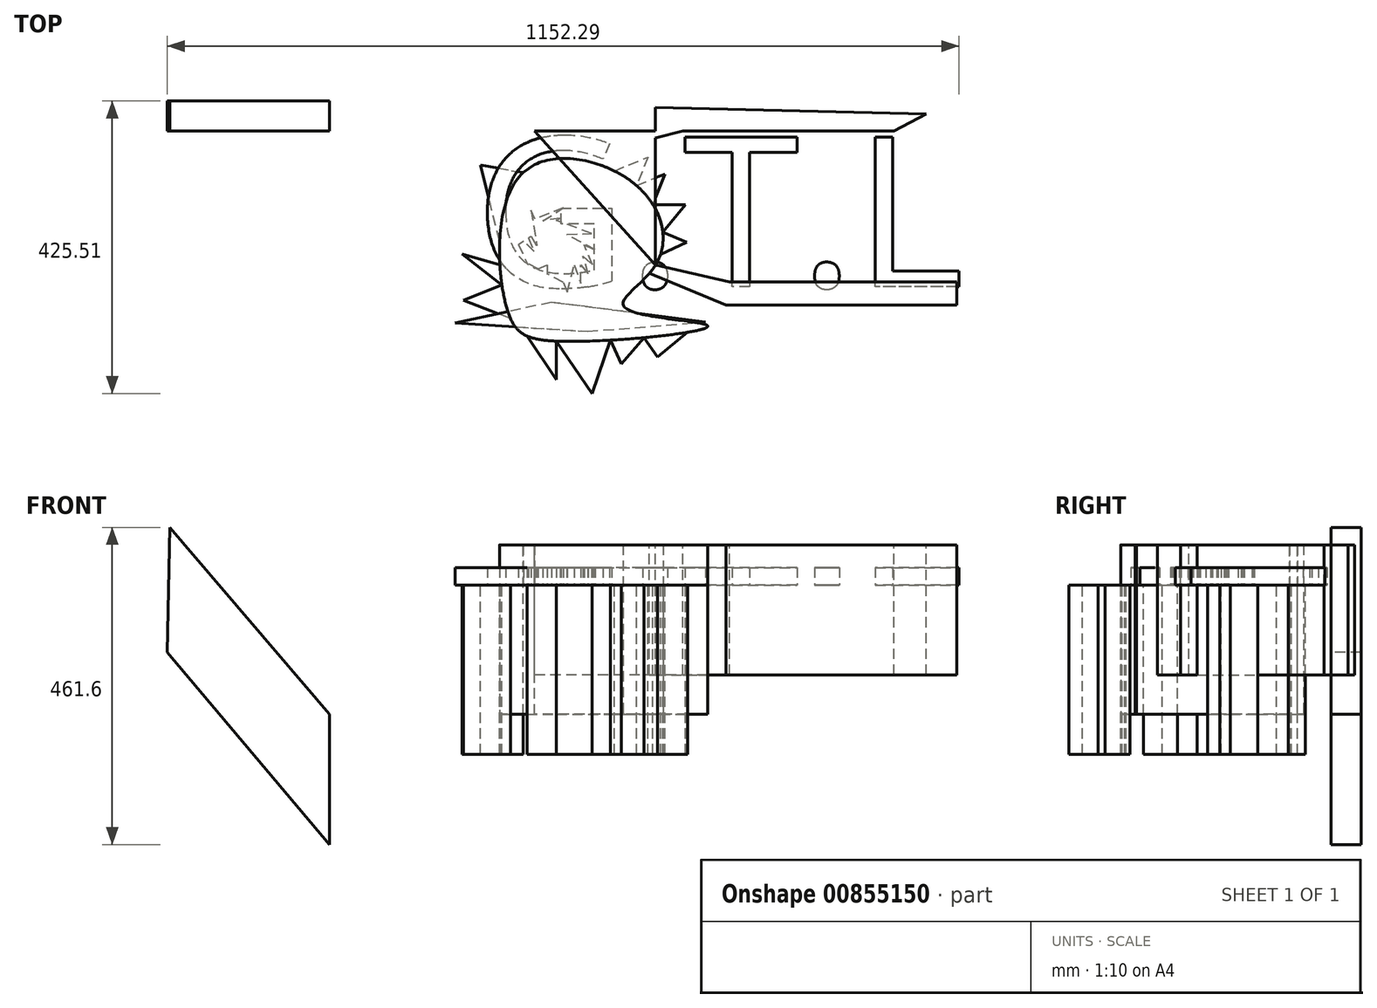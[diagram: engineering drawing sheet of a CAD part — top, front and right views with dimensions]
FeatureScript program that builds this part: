
annotation { "Feature Type Name" : "Feature", "Feature Type Description" : "" }
export const myFeature = defineFeature(function(context is Context, id is Id, definition is map)
    precondition{}
    {
        {
            var Q0;
            Q0=qCreatedBy(makeId("Top.planeOp"),FACE);
            var sketch = newSketch(context, id + "F0", { "sketchPlane" : qUnion([Q0])});
            skCircle(sketch, "E0.cCircle", {"center": v(-8.8, 21.17) * mm, "radius": 64.91 * mm, "construction": true});
            skLineSegment(sketch, "E0.0", {"start": v(25.69, -33.83) * mm, "end": v(-73.67, 18.8) * mm});
            skLineSegment(sketch, "E0.1", {"start": v(-73.67, 18.8) * mm, "end": v(21.58, 78.53) * mm});
            skLineSegment(sketch, "E0.2", {"start": v(21.58, 78.53) * mm, "end": v(25.69, -33.83) * mm});
            skLineSegment(sketch, "E1", {"start": v(-8.8, -43.75) * mm, "end": v(0, 0) * mm});
            skLineSegment(sketch, "E2", {"start": v(0, 0) * mm, "end": v(15.37, -39.08) * mm});
            skLineSegment(sketch, "E3", {"start": v(15.37, -39.08) * mm, "end": v(25.69, 0) * mm});
            skLineSegment(sketch, "E4", {"start": v(25.69, 0) * mm, "end": v(35.5, -26.28) * mm});
            skLineSegment(sketch, "E5", {"start": v(35.5, -26.28) * mm, "end": v(35.5, 0) * mm});
            skLineSegment(sketch, "E6", {"start": v(35.5, 0) * mm, "end": v(46.3, -13.14) * mm});
            skPoint(sketch, "E6.endSnap0", {"position": v(35.5, -13.14) * mm});
            skLineSegment(sketch, "E7", {"start": v(46.3, -13.14) * mm, "end": v(38.83, 12.73) * mm});
            skLineSegment(sketch, "E8", {"start": v(38.83, 12.73) * mm, "end": v(52.57, 0) * mm});
            skLineSegment(sketch, "E9", {"start": v(52.57, 0) * mm, "end": v(40.33, 29.47) * mm});
            skLineSegment(sketch, "E10", {"start": v(40.33, 29.47) * mm, "end": v(56.1, 22.26) * mm});
            skLineSegment(sketch, "E11", {"start": v(56.1, 22.26) * mm, "end": v(15.03, 44.44) * mm});
            skLineSegment(sketch, "E12", {"start": v(15.03, 44.44) * mm, "end": v(51.27, 45.76) * mm});
            skLineSegment(sketch, "E13", {"start": v(51.27, 45.76) * mm, "end": v(0, 65) * mm});
            skLineSegment(sketch, "E14", {"start": v(0, 65) * mm, "end": v(30.84, 72.57) * mm});
            skLineSegment(sketch, "E15", {"start": v(30.84, 72.57) * mm, "end": v(-20.16, 64.2) * mm});
            skLineSegment(sketch, "E16", {"start": v(-20.16, 64.2) * mm, "end": v(10.12, 83.26) * mm});
            skLineSegment(sketch, "E17", {"start": v(10.12, 83.26) * mm, "end": v(-31.54, 66.7) * mm});
            skLineSegment(sketch, "E18", {"start": v(-31.54, 66.7) * mm, "end": v(-36.73, 79.76) * mm});
            skLineSegment(sketch, "E19", {"start": v(-36.73, 79.76) * mm, "end": v(-28.6, 28.3) * mm});
            skLineSegment(sketch, "E20", {"start": v(-28.6, 28.3) * mm, "end": v(-52.81, 68.88) * mm});
            skLineSegment(sketch, "E21", {"start": v(-52.81, 68.88) * mm, "end": v(-32.66, 19.88) * mm});
            skPoint(sketch, "E21.endSnap0", {"position": v(-32.66, 54.03) * mm});
            skLineSegment(sketch, "E22", {"start": v(-32.66, 19.88) * mm, "end": v(-65.53, 52.72) * mm});
            skLineSegment(sketch, "E23", {"start": v(-65.53, 52.72) * mm, "end": v(-42.74, 2.41) * mm});
            skPoint(sketch, "E23.endSnap0", {"position": v(-42.74, 44.38) * mm});
            skLineSegment(sketch, "E24", {"start": v(-42.74, 2.41) * mm, "end": v(-70.94, 2.41) * mm});
            skLineSegment(sketch, "E25", {"start": v(-70.94, 2.41) * mm, "end": v(-23.99, -7.52) * mm});
            skLineSegment(sketch, "E26", {"start": v(-23.99, -7.52) * mm, "end": v(-59.26, -19.66) * mm});
            skLineSegment(sketch, "E27", {"start": v(-59.26, -19.66) * mm, "end": v(-13.56, 0) * mm});
            skLineSegment(sketch, "E28", {"start": v(-13.56, 0) * mm, "end": v(-32.2, -39.38) * mm});
            skLineSegment(sketch, "E29", {"start": v(-32.2, -39.38) * mm, "end": v(-13.56, 0) * mm});
            skLineSegment(sketch, "E30", {"start": v(-13.56, 0) * mm, "end": v(-13.56, -50.7) * mm});
            skLineSegment(sketch, "E31", {"start": v(-13.56, -50.7) * mm, "end": v(-13.56, -25.35) * mm});
            skLineSegment(sketch, "E32", {"start": v(-13.56, -25.35) * mm, "end": v(-7.33, -54.3) * mm});
            skLineSegment(sketch, "E33", {"start": v(-7.33, -54.3) * mm, "end": v(-147.81, -84.54) * mm});
            skLineSegment(sketch, "E34", {"start": v(-147.81, -84.54) * mm, "end": v(45.46, -96.55) * mm});
            skLineSegment(sketch, "E35", {"start": v(45.46, -96.55) * mm, "end": v(217.04, -82.88) * mm});
            skLineSegment(sketch, "E36", {"start": v(217.04, -82.88) * mm, "end": v(-7.33, -54.3) * mm});
            skLineSegment(sketch, "E37", {"start": v(-7.33, -54.3) * mm, "end": v(75.52, -50.7) * mm});
            skLineSegment(sketch, "E38", {"start": v(75.52, -50.7) * mm, "end": v(-95.32, -39.38) * mm});
            skLineSegment(sketch, "E39", {"start": v(-95.32, -39.38) * mm, "end": v(-7.33, -54.3) * mm});
            skSolve(sketch);
        }
        {
            var Q0;
            Q0=makeQuery(id+"F0.imprint","IMPRINT",FACE,{"disambiguationData":[TD([[makeQuery(id+"F0.imprint","IMPRINT",EDGE,{"derivedFrom":sQuery(id+"F0.wireOp",EDGE,"E33")}),1.0]])]});
            var Q1;
            {var subQ3=sQuery(id+"F0.wireOp",EDGE,"E0.0");var subQ5=sQuery(id+"F0.wireOp",EDGE,"E3");var subQ6=makeQuery(id+"F0.imprint","INTERSECT",VERTEX,{"derivedFrom":[subQ3,subQ5]});Q1=makeQuery(id+"F0.imprint","IMPRINT",FACE,{"disambiguationData":[TD([[makeQuery(id+"F0.imprint","IMPRINT",EDGE,{"disambiguationData":[TD([[subQ6,-1.0]])],"derivedFrom":subQ3}),-1.0]])]});}
            var Q2;
            {var subQ0=sQuery(id+"F0.wireOp",EDGE,"E16");Q2=makeQuery(id+"F0.imprint","IMPRINT",FACE,{"disambiguationData":[TD([[makeQuery(id+"F0.imprint","IMPRINT",EDGE,{"derivedFrom":subQ0}),1.0]])]});}
            var Q3;
            {var subQ0=sQuery(id+"F0.wireOp",EDGE,"E4");Q3=makeQuery(id+"F0.imprint","IMPRINT",FACE,{"disambiguationData":[TD([[makeQuery(id+"F0.imprint","IMPRINT",EDGE,{"derivedFrom":subQ0}),1.0]])]});}
            var Q4;
            {var subQ0=sQuery(id+"F0.wireOp",EDGE,"E13");var subQ1=sQuery(id+"F0.wireOp",EDGE,"E0.2");var subQ2=makeQuery(id+"F0.imprint","INTERSECT",VERTEX,{"derivedFrom":[subQ1,subQ0]});Q4=makeQuery(id+"F0.imprint","IMPRINT",FACE,{"disambiguationData":[TD([[makeQuery(id+"F0.imprint","IMPRINT",EDGE,{"disambiguationData":[TD([[subQ2,-1.0]])],"derivedFrom":subQ1}),1.0]])]});}
            var Q5;
            {var subQ0=sQuery(id+"F0.wireOp",EDGE,"E3");var subQ1=sQuery(id+"F0.wireOp",EDGE,"E0.0");var subQ2=makeQuery(id+"F0.imprint","INTERSECT",VERTEX,{"derivedFrom":[subQ1,subQ0]});Q5=makeQuery(id+"F0.imprint","IMPRINT",FACE,{"disambiguationData":[TD([[makeQuery(id+"F0.imprint","IMPRINT",EDGE,{"disambiguationData":[TD([[subQ2,-1.0]])],"derivedFrom":subQ1}),1.0]])]});}
            var Q6;
            {var subQ0=sQuery(id+"F0.wireOp",EDGE,"E32");var subQ1=sQuery(id+"F0.wireOp",EDGE,"E31");var subQ2=makeQuery(id+"F0.imprint","INTERSECT",VERTEX,{"derivedFrom":[subQ1,subQ0]});Q6=makeQuery(id+"F0.imprint","IMPRINT",FACE,{"disambiguationData":[TD([[makeQuery(id+"F0.imprint","IMPRINT",EDGE,{"disambiguationData":[TD([[subQ2,1.0]])],"derivedFrom":subQ1}),-1.0]])]});}
            var Q7;
            {var subQ0=sQuery(id+"F0.wireOp",EDGE,"E1");var subQ1=sQuery(id+"F0.wireOp",EDGE,"E0.0");var subQ2=makeQuery(id+"F0.imprint","INTERSECT",VERTEX,{"derivedFrom":[subQ1,subQ0]});Q7=makeQuery(id+"F0.imprint","IMPRINT",FACE,{"disambiguationData":[TD([[makeQuery(id+"F0.imprint","IMPRINT",EDGE,{"disambiguationData":[TD([[subQ2,1.0]])],"derivedFrom":subQ1}),-1.0]])]});}
            extrude(context, id + "F1", {"entities" : qUnion([Q0, Q1, Q2, Q3, Q4, Q5, Q6, Q7]), "depth" : 25.4 * mm, "offsetDistance" : 25.4 * mm});
        }
        {
            var Q0;
            Q0=qCreatedBy(makeId("Top.planeOp"),FACE);
            var sketch = newSketch(context, id + "F2", { "sketchPlane" : qUnion([Q0])});
            skFitSpline(sketch, "E40", {"points": [v(99.08, -61.5) * mm, v(144.18, 0) * mm, v(116.7, 115.52) * mm, v(-48.59, 134.54) * mm, v(-71.2, -66.35) * mm, v(0, -110.78) * mm, v(220.12, -88.25) * mm, v(99.08, -61.5) * mm]});
            skLineSegment(sketch, "E41", {"start": v(84.19, 136.97) * mm, "end": v(133.04, 157.14) * mm});
            skLineSegment(sketch, "E42", {"start": v(133.04, 157.14) * mm, "end": v(116.7, 115.52) * mm});
            skLineSegment(sketch, "E43", {"start": v(116.7, 115.52) * mm, "end": v(157.88, 132.52) * mm});
            skLineSegment(sketch, "E44", {"start": v(157.88, 132.52) * mm, "end": v(140.4, 88) * mm});
            skLineSegment(sketch, "E45", {"start": v(140.4, 88) * mm, "end": v(187.75, 88) * mm});
            skLineSegment(sketch, "E46", {"start": v(187.75, 88) * mm, "end": v(154.72, 47.94) * mm});
            skLineSegment(sketch, "E47", {"start": v(154.72, 47.94) * mm, "end": v(189.92, 33.1) * mm});
            skLineSegment(sketch, "E48", {"start": v(189.92, 33.1) * mm, "end": v(151.45, 15.46) * mm});
            skLineSegment(sketch, "E49", {"start": v(151.45, 15.46) * mm, "end": v(197.55, 0) * mm});
            skLineSegment(sketch, "E50", {"start": v(197.55, 0) * mm, "end": v(131.4, -16.23) * mm});
            skLineSegment(sketch, "E51", {"start": v(131.4, -16.23) * mm, "end": v(196.36, -37.54) * mm});
            skLineSegment(sketch, "E52", {"start": v(196.36, -37.54) * mm, "end": v(99.08, -61.5) * mm});
            skLineSegment(sketch, "E53", {"start": v(99.08, -61.5) * mm, "end": v(190.77, -61.5) * mm});
            skLineSegment(sketch, "E54", {"start": v(190.77, -61.5) * mm, "end": v(190.77, -81.95) * mm});
            skLineSegment(sketch, "E55", {"start": v(190.77, -81.95) * mm, "end": v(224.98, -63.13) * mm});
            skLineSegment(sketch, "E56", {"start": v(224.98, -63.13) * mm, "end": v(220.12, -88.25) * mm});
            skLineSegment(sketch, "E57", {"start": v(220.12, -132.41) * mm, "end": v(220.12, -88.25) * mm});
            skLineSegment(sketch, "E58", {"start": v(220.37, -134.06) * mm, "end": v(190.77, -97.92) * mm});
            skLineSegment(sketch, "E59", {"start": v(190.77, -97.92) * mm, "end": v(146.79, -133.95) * mm});
            skLineSegment(sketch, "E60", {"start": v(146.79, -133.95) * mm, "end": v(127.26, -105.69) * mm});
            skLineSegment(sketch, "E61", {"start": v(127.26, -105.69) * mm, "end": v(94.43, -144.12) * mm});
            skLineSegment(sketch, "E62", {"start": v(94.43, -144.12) * mm, "end": v(78.56, -109.35) * mm});
            skLineSegment(sketch, "E63", {"start": v(78.56, -109.35) * mm, "end": v(51.88, -186.9) * mm});
            skLineSegment(sketch, "E64", {"start": v(51.88, -186.9) * mm, "end": v(0, -110.78) * mm});
            skLineSegment(sketch, "E65", {"start": v(0, -110.78) * mm, "end": v(0, -166.72) * mm});
            skLineSegment(sketch, "E66", {"start": v(0, -166.72) * mm, "end": v(0, -166.72) * mm});
            skLineSegment(sketch, "E67", {"start": v(0, -166.72) * mm, "end": v(-43.03, -103.26) * mm});
            skLineSegment(sketch, "E68", {"start": v(-43.03, -103.26) * mm, "end": v(-93.69, -140.7) * mm});
            skLineSegment(sketch, "E69", {"start": v(-93.69, -140.7) * mm, "end": v(-66.89, -77.95) * mm});
            skLineSegment(sketch, "E70", {"start": v(-66.89, -77.95) * mm, "end": v(-135.48, -51.1) * mm});
            skLineSegment(sketch, "E71", {"start": v(-135.48, -51.1) * mm, "end": v(-79.46, -28.78) * mm});
            skLineSegment(sketch, "E72", {"start": v(-79.46, -28.78) * mm, "end": v(-137.06, 16.26) * mm});
            skLineSegment(sketch, "E73", {"start": v(-137.06, 16.26) * mm, "end": v(-82.4, 0) * mm});
            skLineSegment(sketch, "E74", {"start": v(-82.4, 0) * mm, "end": v(-126.54, 90.9) * mm});
            skLineSegment(sketch, "E75", {"start": v(-126.54, 90.9) * mm, "end": v(-82.68, 35.12) * mm});
            skLineSegment(sketch, "E76", {"start": v(-82.68, 35.12) * mm, "end": v(-110.6, 145.72) * mm});
            skLineSegment(sketch, "E77", {"start": v(-110.6, 145.72) * mm, "end": v(-48.59, 134.54) * mm});
            skLineSegment(sketch, "E78", {"start": v(-48.59, 134.54) * mm, "end": v(21.4, 182.68) * mm});
            skLineSegment(sketch, "E79", {"start": v(21.4, 182.68) * mm, "end": v(64, 145.57) * mm});
            skLineSegment(sketch, "E80", {"start": v(64, 145.57) * mm, "end": v(98.83, 182.42) * mm});
            skLineSegment(sketch, "E81", {"start": v(98.83, 182.42) * mm, "end": v(84.19, 136.97) * mm});
            skSolve(sketch);
        }
        {
            var Q0;
            {var subQ0=sQuery(id+"F2.wireOp",EDGE,"E40");var subQ6=makeQuery(id+"F2.imprint","INTERSECT",VERTEX,{"derivedFrom":[subQ0,sQuery(id+"F2.wireOp",EDGE,"E41")]});Q0=makeQuery(id+"F2.imprint","IMPRINT",FACE,{"disambiguationData":[TD([[makeQuery(id+"F2.imprint","IMPRINT",EDGE,{"disambiguationData":[TD([[subQ6,-1.0]])],"derivedFrom":subQ0}),1.0]])]});}
            var sketch = newSketch(context, id + "F3", { "sketchPlane" : qUnion([Q0])});
            skSolve(sketch);
        }
        {
            var Q0;
            {var subQ0=sQuery(id+"F2.wireOp",EDGE,"E40");var subQ20=makeQuery(id+"F2.imprint","INTERSECT",VERTEX,{"derivedFrom":[subQ0,sQuery(id+"F2.wireOp",EDGE,"E59")]});Q0=makeQuery(id+"F3.imprint","IMPRINT",FACE,{"disambiguationData":[TD([[makeQuery(id+"F3.imprint","IMPRINT",EDGE,{"derivedFrom":makeQuery(id+"F2.imprint","IMPRINT",EDGE,{"disambiguationData":[TD([[subQ20,-1.0]])],"derivedFrom":subQ0})}),1.0]])]});}
            extrude(context, id + "F4", {"entities" : qUnion([Q0]), "depth" : 58.4 * mm, "offsetDistance" : 25.4 * mm});
        }
        {
            var Q0;
            {var subQ0=sQuery(id+"F2.wireOp",EDGE,"E63");Q0=makeQuery(id+"F2.imprint","IMPRINT",FACE,{"disambiguationData":[TD([[makeQuery(id+"F2.imprint","IMPRINT",EDGE,{"derivedFrom":subQ0}),-1.0]])]});}
            var Q1;
            {var subQ0=sQuery(id+"F2.wireOp",EDGE,"E61");Q1=makeQuery(id+"F2.imprint","IMPRINT",FACE,{"disambiguationData":[TD([[makeQuery(id+"F2.imprint","IMPRINT",EDGE,{"derivedFrom":subQ0}),-1.0]])]});}
            var Q2;
            {var subQ0=sQuery(id+"F2.wireOp",EDGE,"E59");Q2=makeQuery(id+"F2.imprint","IMPRINT",FACE,{"disambiguationData":[TD([[makeQuery(id+"F2.imprint","IMPRINT",EDGE,{"derivedFrom":subQ0}),-1.0]])]});}
            var Q3;
            {var subQ0=sQuery(id+"F2.wireOp",EDGE,"E65");Q3=makeQuery(id+"F2.imprint","IMPRINT",FACE,{"disambiguationData":[TD([[makeQuery(id+"F2.imprint","IMPRINT",EDGE,{"derivedFrom":subQ0}),-1.0]])]});}
            var Q4;
            {var subQ0=sQuery(id+"F2.wireOp",EDGE,"E47");Q4=makeQuery(id+"F2.imprint","IMPRINT",FACE,{"disambiguationData":[TD([[makeQuery(id+"F2.imprint","IMPRINT",EDGE,{"derivedFrom":subQ0}),-1.0]])]});}
            var Q5;
            {var subQ0=sQuery(id+"F2.wireOp",EDGE,"E45");Q5=makeQuery(id+"F2.imprint","IMPRINT",FACE,{"disambiguationData":[TD([[makeQuery(id+"F2.imprint","IMPRINT",EDGE,{"derivedFrom":subQ0}),-1.0]])]});}
            var Q6;
            {var subQ0=sQuery(id+"F2.wireOp",EDGE,"E43");Q6=makeQuery(id+"F2.imprint","IMPRINT",FACE,{"disambiguationData":[TD([[makeQuery(id+"F2.imprint","IMPRINT",EDGE,{"derivedFrom":subQ0}),-1.0]])]});}
            var Q7;
            Q7=makeQuery(id+"F4.opExtrude","CAP_FACE",FACE,{"disambiguationData":[OSD([sQuery(id+"F2.wireOp",EDGE,"E40"),sQuery(id+"F2.wireOp",EDGE,"E57"),sQuery(id+"F2.wireOp",EDGE,"E78")])],"isStart":false});
            var Q8;
            {var subQ0=sQuery(id+"F2.wireOp",EDGE,"E41");Q8=makeQuery(id+"F2.imprint","IMPRINT",FACE,{"disambiguationData":[TD([[makeQuery(id+"F2.imprint","IMPRINT",EDGE,{"derivedFrom":subQ0}),-1.0]])]});}
            var Q9;
            {var subQ0=sQuery(id+"F2.wireOp",EDGE,"E72");Q9=makeQuery(id+"F2.imprint","IMPRINT",FACE,{"disambiguationData":[TD([[makeQuery(id+"F2.imprint","IMPRINT",EDGE,{"derivedFrom":subQ0}),-1.0]])]});}
            var Q10;
            {var subQ0=sQuery(id+"F2.wireOp",EDGE,"E70");Q10=makeQuery(id+"F2.imprint","IMPRINT",FACE,{"disambiguationData":[TD([[makeQuery(id+"F2.imprint","IMPRINT",EDGE,{"derivedFrom":subQ0}),-1.0]])]});}
            var Q11;
            {var subQ0=sQuery(id+"F2.wireOp",EDGE,"E76");Q11=makeQuery(id+"F2.imprint","IMPRINT",FACE,{"disambiguationData":[TD([[makeQuery(id+"F2.imprint","IMPRINT",EDGE,{"derivedFrom":subQ0}),-1.0]])]});}
            extrude(context, id + "F5", {"entities" : qUnion([Q0, Q1, Q2, Q3, Q4, Q5, Q6, Q7, Q8, Q9, Q10, Q11]), "oppositeDirection" : true, "depth" : 246.74 * mm, "offsetDistance" : 25.4 * mm});
        }
        {
            var Q0;
            Q0=qCreatedBy(makeId("Top.planeOp"),FACE);
            var sketch = newSketch(context, id + "F6", { "sketchPlane" : qUnion([Q0])});
            skText(sketch, "E82", { "text": "G.T.L", "fontName": "OpenSans-Regular.ttf"});
            const initialGuessF6  = {"E82": [-0.11925, -0.03166, 1, 0, 0.21978]};
            skSetInitialGuess(sketch, initialGuessF6);
            skSolve(sketch);
        }
        {
            var Q0;
            Q0 = qSketchRegion(id + "F6", true);
            extrude(context, id + "F7", {"entities" : qUnion([Q0]), "depth" : 25.4 * mm, "offsetDistance" : 25.4 * mm});
        }
        {
            var Q0;
            Q0=makeQuery(id+"F5.opExtrude","CAP_FACE",FACE,{"disambiguationData":[OSD([sQuery(id+"F2.wireOp",EDGE,"E40"),sQuery(id+"F2.wireOp",EDGE,"E57"),sQuery(id+"F2.wireOp",EDGE,"E78")])],"isStart":true});
            var sketch = newSketch(context, id + "F8", { "sketchPlane" : qUnion([Q0])});
            skLineSegment(sketch, "E83", {"start": v(-48.59, 134.54) * mm, "end": v(184.04, 195.19) * mm});
            skLineSegment(sketch, "E84", {"start": v(184.04, 195.19) * mm, "end": v(491.3, 195.19) * mm});
            skLineSegment(sketch, "E85", {"start": v(491.3, 195.19) * mm, "end": v(-31.94, 195.19) * mm});
            skLineSegment(sketch, "E86", {"start": v(-31.94, 195.19) * mm, "end": v(144.18, 0) * mm});
            skLineSegment(sketch, "E87", {"start": v(144.18, 0) * mm, "end": v(252.18, -24.46) * mm});
            skLineSegment(sketch, "E88", {"start": v(252.18, -24.46) * mm, "end": v(582.45, -24.46) * mm});
            skLineSegment(sketch, "E89", {"start": v(582.45, -24.46) * mm, "end": v(582.45, -58.05) * mm});
            skLineSegment(sketch, "E90", {"start": v(582.45, -58.05) * mm, "end": v(246.76, -58.05) * mm});
            skLineSegment(sketch, "E91", {"start": v(246.76, -58.05) * mm, "end": v(135, -12.23) * mm});
            skPoint(sketch, "E91.endSnap0", {"position": v(198.18, -12.23) * mm});
            skLineSegment(sketch, "E92", {"start": v(135, -12.23) * mm, "end": v(135, -12.23) * mm});
            skLineSegment(sketch, "E93", {"start": v(144.18, 0) * mm, "end": v(144.18, 229.4) * mm});
            skLineSegment(sketch, "E94", {"start": v(144.18, 229.4) * mm, "end": v(538.02, 219.83) * mm});
            skLineSegment(sketch, "E95", {"start": v(538.02, 219.83) * mm, "end": v(491.3, 195.19) * mm});
            skSolve(sketch);
        }
        {
            var Q0;
            Q0 = qSketchRegion(id + "F8", true);
            var Q1;
            {var subQ0=sQuery(id+"F8.wireOp",EDGE,"E87");Q1=makeQuery(id+"F8.imprint","IMPRINT",FACE,{"disambiguationData":[TD([[makeQuery(id+"F8.imprint","IMPRINT",EDGE,{"derivedFrom":subQ0}),-1.0]])]});}
            extrude(context, id + "F9", {"entities" : qUnion([Q0, Q1]), "oppositeDirection" : true, "depth" : 189.26 * mm, "offsetDistance" : 25.4 * mm});
        }
        {
            var Q0;
            {var subQ0=sQuery(id+"F8.wireOp",EDGE,"E85");Q0=makeQuery(id+"F9.opExtrude","SWEPT_FACE",FACE,{"disambiguationData":[OSD([subQ0]),TDD([makeQuery(id+"F8.imprint","IMPRINT",EDGE,{"disambiguationData":[TD([[makeQuery(id+"F8.imprint","INTERSECT",VERTEX,{"derivedFrom":[sQuery(id+"F8.wireOp",EDGE,"E83"),subQ0]}),1.0]])],"derivedFrom":subQ0})])]});}
            var sketch = newSketch(context, id + "F10", { "sketchPlane" : qUnion([Q0])});
            skLineSegment(sketch, "E96", {"start": v(563.12, 83.74) * mm, "end": v(330.53, -187.98) * mm});
            skLineSegment(sketch, "E97", {"start": v(330.53, -187.98) * mm, "end": v(330.53, -377.86) * mm});
            skLineSegment(sketch, "E98", {"start": v(330.53, -377.86) * mm, "end": v(566.56, -98.18) * mm});
            skLineSegment(sketch, "E99", {"start": v(566.56, -98.18) * mm, "end": v(563.12, 83.74) * mm});
            skSolve(sketch);
        }
        {
            var Q0;
            Q0 = qSketchRegion(id + "F10", true);
            extrude(context, id + "F11", {"entities" : qUnion([Q0]), "operationType" : NewBodyOperationType.ADD, "depth" : 43.42 * mm, "offsetDistance" : 25.4 * mm});
        }
    });
